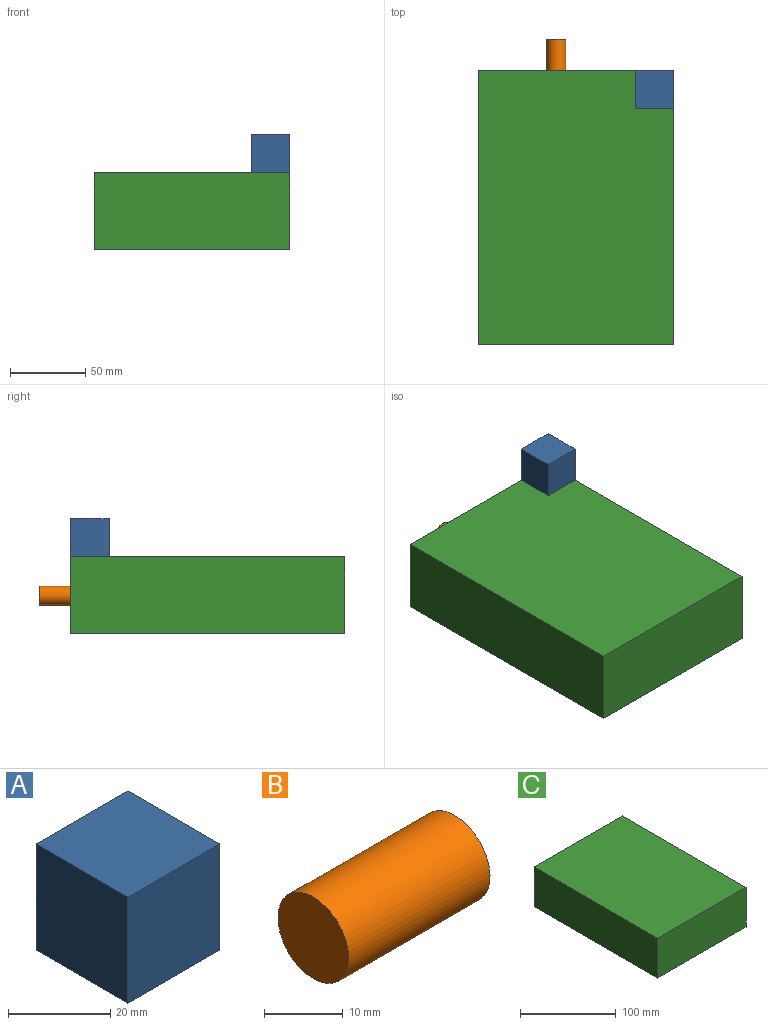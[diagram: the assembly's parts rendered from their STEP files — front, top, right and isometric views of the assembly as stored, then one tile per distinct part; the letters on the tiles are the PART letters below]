
ASSEMBLY  parts=3 mates=2
PART A: 6 faces, bbox 25.4x25.4x25.4 mm
  f0: plane 25.4x25.4mm, normal (0,1,0), area 645.2mm2, adj f1,f3,f4,f5
  f1: plane 25.4x25.4mm, normal (-1,0,0), area 645.2mm2, adj f0,f2,f4,f5
  f2: plane 25.4x25.4mm, normal (0,-1,0), area 645.2mm2, adj f1,f3,f4,f5
  f3: plane 25.4x25.4mm, normal (1,0,0), area 645.2mm2, adj f0,f2,f4,f5
  f4: plane 25.4x25.4mm, normal (0,0,1), area 645.2mm2, adj f0,f1,f2,f3
  f5: plane 25.4x25.4mm, normal (0,0,-1), area 645.2mm2, adj f0,f1,f2,f3
PART B: 3 faces, bbox 25.4x12.7x12.7 mm
  f0: cylinder r=6.35mm len=25.4mm, axis (-1,0,0), area 1013.4mm2, adj f1,f2
  f1: plane 12.7x12.7mm, normal (1,0,0), area 126.7mm2, adj f0
  f2: plane 12.7x12.7mm, normal (-1,0,0), area 126.7mm2, adj f0
PART C: 8 faces, bbox 130.2x182.5x50.8 mm
  f0: plane 182.55x50.8mm, normal (1,0,0), area 9273.4mm2, adj f1,f3,f4,f5
  f1: plane 130.24x50.8mm, normal (0,1,0), area 5596.8mm2, adj f0,f2,f4,f5,f6
  f2: plane 182.55x50.8mm, normal (-1,0,0), area 9273.4mm2, adj f1,f3,f4,f5
  f3: plane 130.24x50.8mm, normal (0,-1,0), area 6616.2mm2, adj f0,f2,f4,f5
  f4: plane 182.55x130.24mm, normal (0,0,1), area 23775mm2, adj f0,f1,f2,f3
  f5: plane 182.55x130.24mm, normal (0,0,-1), area 23775mm2, adj f0,f1,f2,f3
  f6: cylinder r=18.01mm len=36.03mm, axis (0,1,0), area 2874.8mm2, adj f1,f7
  f7: plane 36.03x36.03mm, normal (0,1,0), area 1019.4mm2, adj f6
PLACE A t=(2.09,81.72,25.68)mm
PLACE B rot(axis=(0.58,0.58,0.58),120deg) t=(-63.88,90.21,-0.15)mm
PLACE C t=(-50.85,3.15,-25.12)mm
MATE fastened A.f5 <-> C.f4  axis (0,0,1) through (14.27,94.42,25.68)mm
MATE slider B.f0 <-> C.f6  axis (0,1,0) through (-63.88,115.61,-0.15)mm
